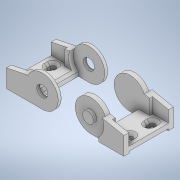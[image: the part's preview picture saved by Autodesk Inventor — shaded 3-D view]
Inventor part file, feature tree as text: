
AUTODESK INVENTOR PART (.ipt)
format: ipt  version: 2020 (Build 240168000, 168)  size: 201,216 bytes
history: native  units: in
note: dims shown in document units (in); Inventor stores cm internally (conversion verified against a paired STEP export)
features: mirror x1, other x1
ambient origin geometry x8: Origin, YZ Plane, XZ Plane, XY Plane, X Axis, Y Axis, Z Axis, Center Point
bodies: Solid1 (feature_tree), Solid2 (feature_tree)
feature tree (2):
  mirror  "Mirror1"
  other  "Cut-Extrude8"
